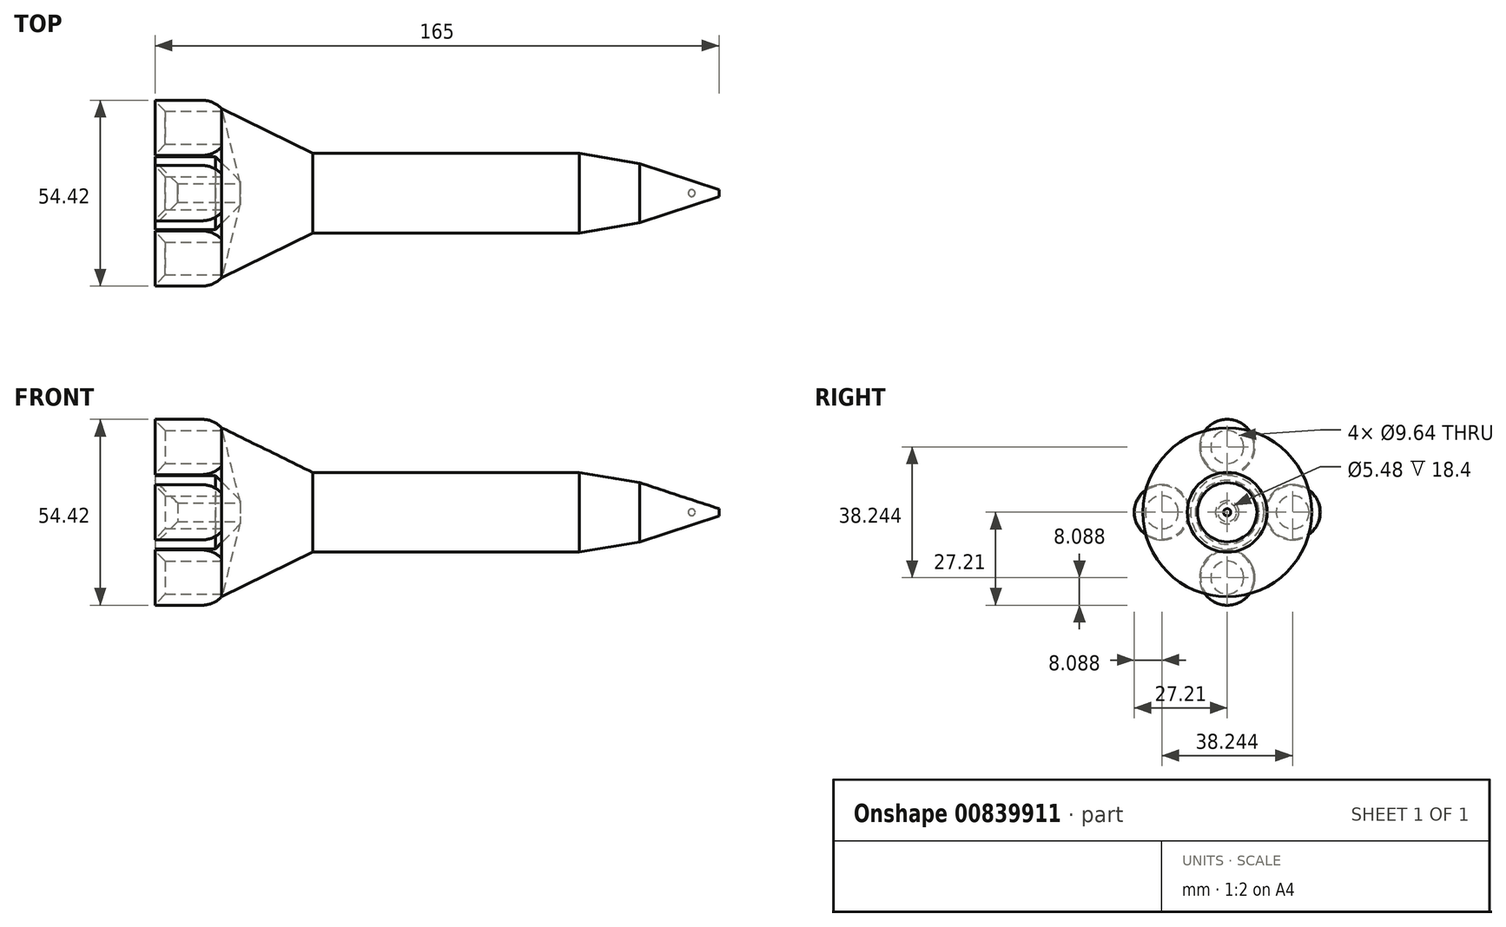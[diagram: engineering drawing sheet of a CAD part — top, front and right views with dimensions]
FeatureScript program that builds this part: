
annotation { "Feature Type Name" : "Feature", "Feature Type Description" : "" }
export const myFeature = defineFeature(function(context is Context, id is Id, definition is map)
    precondition{}
    {
        {
            var Q0;
            Q0=qCreatedBy(makeId("Front.planeOp"),FACE);
            var sketch = newSketch(context, id + "F0", { "sketchPlane" : qUnion([Q0])});
            skLineSegment(sketch, "E0", {"start": v(-74.3, 0) * mm, "end": v(65.7, 0) * mm});
            skLineSegment(sketch, "E1", {"start": v(65.7, 0) * mm, "end": v(65.7, 1.05) * mm});
            skLineSegment(sketch, "E2", {"start": v(65.7, 1.05) * mm, "end": v(42.46, 8.67) * mm});
            skLineSegment(sketch, "E3", {"start": v(42.46, 8.67) * mm, "end": v(24.85, 11.67) * mm});
            skLineSegment(sketch, "E4", {"start": v(24.85, 11.67) * mm, "end": v(-53.41, 11.67) * mm});
            skLineSegment(sketch, "E5", {"start": v(-52.45, 11.3) * mm, "end": v(-53.41, 11.67) * mm});
            skLineSegment(sketch, "E6", {"start": v(-52.45, 11.3) * mm, "end": v(-74.3, 2.74) * mm});
            skLineSegment(sketch, "E7", {"start": v(-74.3, 2.74) * mm, "end": v(-74.3, 0) * mm});
            skCircle(sketch, "E8", {"center": v(57.7, 0) * mm, "radius": 1 * mm});
            skLineSegment(sketch, "E9", {"start": v(-52.45, 11.3) * mm, "end": v(-79.76, 24.72) * mm});
            skLineSegment(sketch, "E10", {"start": v(-79.76, 24.72) * mm, "end": v(-74.3, 2.74) * mm});
            skSolve(sketch);
        }
        {
            var Q0;
            Q0=qSketchRegion(id+"F0",true);
            var Q1;
            Q1=sQuery(id+"F0.wireOp",EDGE,"E0");
            revolve(context, id + "F1", {"surfaceOperationType" : NewSurfaceOperationType.NEW, "entities" : qUnion([Q0]), "axis" : qUnion([Q1]), "revolveType" : RevolveType.FULL});
        }
        {
            var Q0;
            Q0=makeQuery(id+"F1.opRevolve","SWEPT_FACE",FACE,{"disambiguationData":[OSD([sQuery(id+"F0.wireOp",EDGE,"E7")])]});
            var sketch = newSketch(context, id + "F2", { "sketchPlane" : qUnion([Q0])});
            skCircle(sketch, "E11", {"center": v(0, 0) * mm, "radius": 10.72 * mm});
            skCircle(sketch, "E12", {"center": v(-19.12, 0) * mm, "radius": 8.1 * mm});
            skCircle(sketch, "E13.1.0", {"center": v(0, -19.12) * mm, "radius": 8.1 * mm});
            skCircle(sketch, "E13.2.0", {"center": v(19.12, 0) * mm, "radius": 8.1 * mm});
            skCircle(sketch, "E13.3.0", {"center": v(0, 19.12) * mm, "radius": 8.1 * mm});
            skCircle(sketch, "E14", {"center": v(0, -19.12) * mm, "radius": 4.82 * mm});
            skCircle(sketch, "E15.1.0", {"center": v(19.12, 0) * mm, "radius": 4.82 * mm});
            skCircle(sketch, "E15.2.0", {"center": v(0, 19.12) * mm, "radius": 4.82 * mm});
            skCircle(sketch, "E16.1.3.0", {"center": v(-19.12, 0) * mm, "radius": 4.82 * mm});
            skSolve(sketch);
        }
        {
            var Q0;
            Q0=makeQuery(id+"F2.imprint","IMPRINT",FACE,{"disambiguationData":[TD([[makeQuery(id+"F2.imprint","IMPRINT",EDGE,{"derivedFrom":sQuery(id+"F2.wireOp",EDGE,"E11")}),1.0]])]});
            extrude(context, id + "F3", {"entities" : qUnion([Q0]), "depth" : 25 * mm, "offsetDistance" : 25 * mm});
        }
        {
            var Q0;
            Q0=makeQuery(id+"F3.opExtrude","CAP_EDGE",EDGE,{"disambiguationData":[OSD([sQuery(id+"F0.wireOp",EDGE,"E6"),sQuery(id+"F0.wireOp",EDGE,"E7")])],"isStart":false});
            chamfer(context, id + "F4", {"entities" : qUnion([Q0]), "width" : 6.6 * mm, "tangentPropagation" : true});
        }
        {
            var Q0;
            Q0=makeQuery(id+"F3.opExtrude","CAP_EDGE",EDGE,{"disambiguationData":[OSD([sQuery(id+"F2.wireOp",EDGE,"E11")])],"isStart":true});
            chamfer(context, id + "F5", {"entities" : qUnion([Q0]), "width" : 7.3 * mm, "tangentPropagation" : true});
        }
        {
            var Q0;
            Q0 = qSketchRegion(id + "F2", true);
            extrude(context, id + "F6", {"entities" : qUnion([Q0]), "depth" : 25 * mm, "offsetDistance" : 25 * mm});
        }
        {
            var Q0;
            Q0=makeQuery(id+"F6.opExtrude","SWEPT_BODY",BODY,{"disambiguationData":[OSD([sQuery(id+"F2.wireOp",EDGE,"E11")])]});
            deleteBodies(context, id + "F7", {"entities" : qUnion([Q0])});
        }
        {
            var Q0;
            Q0=makeQuery(id+"F6.opExtrude","CAP_EDGE",EDGE,{"disambiguationData":[OSD([sQuery(id+"F2.wireOp",EDGE,"E13.2.0")])],"isStart":true});
            var Q1;
            Q1=makeQuery(id+"F6.opExtrude","CAP_EDGE",EDGE,{"disambiguationData":[OSD([sQuery(id+"F2.wireOp",EDGE,"E13.3.0")])],"isStart":true});
            var Q2;
            Q2=makeQuery(id+"F6.opExtrude","CAP_EDGE",EDGE,{"disambiguationData":[OSD([sQuery(id+"F2.wireOp",EDGE,"E13.1.0")])],"isStart":true});
            var Q3;
            Q3=makeQuery(id+"F6.opExtrude","CAP_EDGE",EDGE,{"disambiguationData":[OSD([sQuery(id+"F2.wireOp",EDGE,"E12")])],"isStart":true});
            chamfer(context, id + "F8", {"entities" : qUnion([Q0, Q1, Q2, Q3]), "width" : 8 * mm, "tangentPropagation" : true});
        }
        {
            var Q0;
            Q0=makeQuery(id+"F8.opChamfer","BLEND_EDGE",EDGE,{"blendedFrom":[makeQuery(id+"F6.opExtrude","CAP_EDGE",EDGE,{"disambiguationData":[OSD([sQuery(id+"F2.wireOp",EDGE,"E13.2.0")])],"isStart":true}),makeQuery(id+"F6.opExtrude","SWEPT_FACE",FACE,{"disambiguationData":[OSD([sQuery(id+"F2.wireOp",EDGE,"E15.1.0")])]})],"blendedInto":[makeQuery(id+"F6.opExtrude","SWEPT_FACE",FACE,{"disambiguationData":[OSD([sQuery(id+"F2.wireOp",EDGE,"E15.1.0")])]})]});
            var Q1;
            Q1=makeQuery(id+"F8.opChamfer","BLEND_EDGE",EDGE,{"blendedFrom":[makeQuery(id+"F6.opExtrude","CAP_EDGE",EDGE,{"disambiguationData":[OSD([sQuery(id+"F2.wireOp",EDGE,"E13.3.0")])],"isStart":true}),makeQuery(id+"F6.opExtrude","SWEPT_FACE",FACE,{"disambiguationData":[OSD([sQuery(id+"F2.wireOp",EDGE,"E15.2.0")])]})],"blendedInto":[makeQuery(id+"F6.opExtrude","SWEPT_FACE",FACE,{"disambiguationData":[OSD([sQuery(id+"F2.wireOp",EDGE,"E15.2.0")])]})]});
            var Q2;
            Q2=makeQuery(id+"F8.opChamfer","BLEND_EDGE",EDGE,{"blendedFrom":[makeQuery(id+"F6.opExtrude","CAP_EDGE",EDGE,{"disambiguationData":[OSD([sQuery(id+"F2.wireOp",EDGE,"E13.1.0")])],"isStart":true}),makeQuery(id+"F6.opExtrude","SWEPT_FACE",FACE,{"disambiguationData":[OSD([sQuery(id+"F2.wireOp",EDGE,"E14")])]})],"blendedInto":[makeQuery(id+"F6.opExtrude","SWEPT_FACE",FACE,{"disambiguationData":[OSD([sQuery(id+"F2.wireOp",EDGE,"E14")])]})]});
            var Q3;
            Q3=makeQuery(id+"F8.opChamfer","BLEND_EDGE",EDGE,{"blendedFrom":[makeQuery(id+"F6.opExtrude","CAP_EDGE",EDGE,{"disambiguationData":[OSD([sQuery(id+"F2.wireOp",EDGE,"E12")])],"isStart":true}),makeQuery(id+"F6.opExtrude","SWEPT_FACE",FACE,{"disambiguationData":[OSD([sQuery(id+"F2.wireOp",EDGE,"E16.1.3.0")])]})],"blendedInto":[makeQuery(id+"F6.opExtrude","SWEPT_FACE",FACE,{"disambiguationData":[OSD([sQuery(id+"F2.wireOp",EDGE,"E16.1.3.0")])]})]});
            fillet(context, id + "F9", {"entities" : qUnion([Q0, Q1, Q2, Q3]), "radius" : 0.56 * mm, "tangentPropagation" : true, "allowEdgeOverflow" : false});
        }
        {
            var Q0;
            Q0=makeQuery(id+"F8.opChamfer","BLEND_FACE",FACE,{"disambiguationData":[OSD([sQuery(id+"F2.wireOp",EDGE,"E13.2.0")])]});
            var Q1;
            {var subQ0=sQuery(id+"F2.wireOp",EDGE,"E13.3.0");Q1=makeQuery(id+"F8.opChamfer","BLEND_EDGE",EDGE,{"blendedFrom":[makeQuery(id+"F6.opExtrude","CAP_EDGE",EDGE,{"disambiguationData":[OSD([subQ0])],"isStart":true}),makeQuery(id+"F6.opExtrude","SWEPT_FACE",FACE,{"disambiguationData":[OSD([subQ0])]})],"blendedInto":[makeQuery(id+"F6.opExtrude","SWEPT_FACE",FACE,{"disambiguationData":[OSD([subQ0])]})]});}
            var Q2;
            Q2=makeQuery(id+"F8.opChamfer","BLEND_FACE",FACE,{"disambiguationData":[OSD([sQuery(id+"F2.wireOp",EDGE,"E13.1.0")])]});
            var Q3;
            {var subQ0=sQuery(id+"F2.wireOp",EDGE,"E12");Q3=makeQuery(id+"F8.opChamfer","BLEND_EDGE",EDGE,{"blendedFrom":[makeQuery(id+"F6.opExtrude","CAP_EDGE",EDGE,{"disambiguationData":[OSD([subQ0])],"isStart":true}),makeQuery(id+"F6.opExtrude","SWEPT_FACE",FACE,{"disambiguationData":[OSD([subQ0])]})],"blendedInto":[makeQuery(id+"F6.opExtrude","SWEPT_FACE",FACE,{"disambiguationData":[OSD([subQ0])]})]});}
            fillet(context, id + "F10", {"entities" : qUnion([Q0, Q1, Q2, Q3]), "radius" : 7.9 * mm, "tangentPropagation" : true, "allowEdgeOverflow" : false});
        }
        {
            var Q0;
            Q0=makeQuery(id+"F6.opExtrude","CAP_EDGE",EDGE,{"disambiguationData":[OSD([sQuery(id+"F2.wireOp",EDGE,"E14")])],"isStart":false});
            var Q1;
            Q1=makeQuery(id+"F6.opExtrude","CAP_EDGE",EDGE,{"disambiguationData":[OSD([sQuery(id+"F2.wireOp",EDGE,"E16.1.3.0")])],"isStart":false});
            var Q2;
            Q2=makeQuery(id+"F6.opExtrude","CAP_EDGE",EDGE,{"disambiguationData":[OSD([sQuery(id+"F2.wireOp",EDGE,"E15.1.0")])],"isStart":false});
            var Q3;
            Q3=makeQuery(id+"F6.opExtrude","CAP_EDGE",EDGE,{"disambiguationData":[OSD([sQuery(id+"F2.wireOp",EDGE,"E15.2.0")])],"isStart":false});
            chamfer(context, id + "F11", {"entities" : qUnion([Q0, Q1, Q2, Q3]), "width" : 3 * mm, "tangentPropagation" : true});
        }
    });
